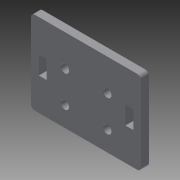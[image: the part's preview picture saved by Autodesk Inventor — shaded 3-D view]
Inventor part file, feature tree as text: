
AUTODESK INVENTOR PART (.ipt)
format: ipt  version: 2013 (Build 170138000, 138)  size: 111,104 bytes
history: native  units: in
note: dims shown in document units (in); Inventor stores cm internally (conversion verified against a paired STEP export)
features: sketch x4, reference x4, extrude x3, fillet x1
ambient origin geometry x8: Origin, YZ Plane, XZ Plane, XY Plane, X Axis, Y Axis, Z Axis, Center Point
bodies: Solid1 (feature_tree)
feature tree (12):
  extrude  "Extrusion1"  Depth=2.638in
  sketch  "Sketch2"  dims[d2=90.0deg d3=0.25in d4=0.0in d5=1.031in]
  extrude  "Extrusion2"  Depth=0.25in TaperAngle=0.0deg
  fillet  "Fillet1"  Radius=1.031in
  extrude  "Extrusion3"  Depth=0.577in
  sketch  "Sketch1"  dims[d0=3.5in d1=2.638in]
  sketch  "Sketch3"  dims[d6=0.25in d7=0.577in]
  sketch  "Sketch4"  dims[d8=0.25in d9=0.25in d10=0.25in d11=0.577in d12=1.0in d13=0.0in d14=0.125in d15=1.0in d16=0.0in]
  reference  "Reference1"
  reference  "Reference2"
  reference  "Reference3"
  reference  "Reference4"
